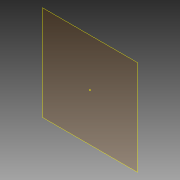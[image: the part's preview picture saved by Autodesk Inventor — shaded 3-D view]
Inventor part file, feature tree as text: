
AUTODESK INVENTOR PART (.ipt)
format: ipt  version: 2015 (Build 190159000, 159)  size: 64,000 bytes
history: native  units: in
note: dims shown in document units (in); Inventor stores cm internally (conversion verified against a paired STEP export)
features: plane x1, sketch x1, other x1
ambient origin geometry x8: Origin, YZ Plane, XZ Plane, XY Plane, X Axis, Y Axis, Z Axis, Center Point
feature tree (3):
  plane  "Work Plane1"
  sketch  "Sketch1"
  other  "Work Point3"
